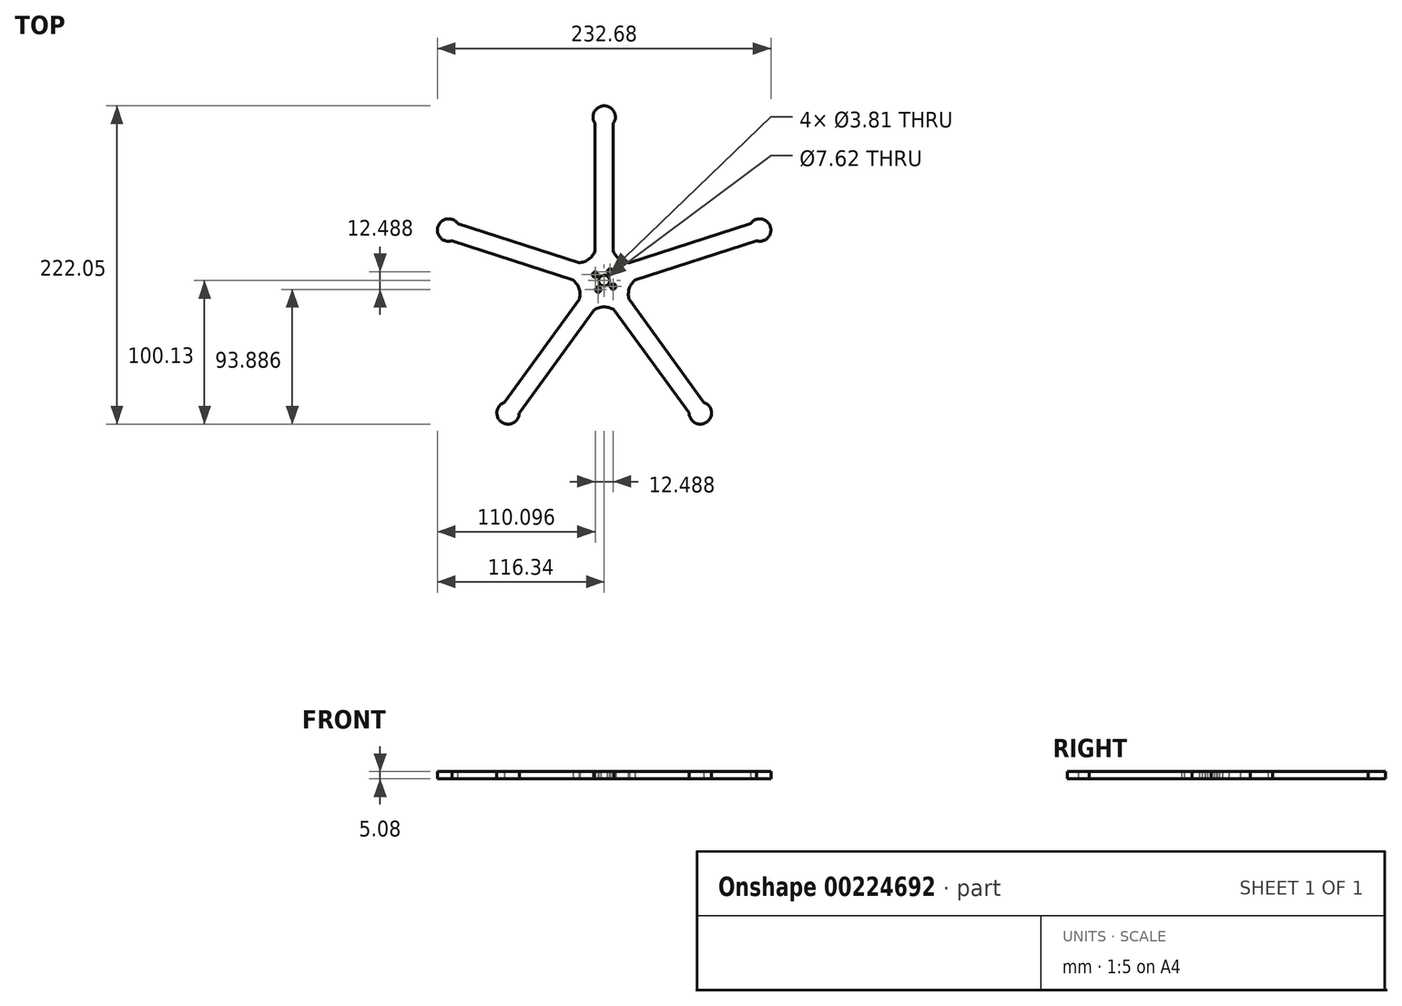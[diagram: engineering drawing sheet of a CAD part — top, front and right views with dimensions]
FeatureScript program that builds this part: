
annotation { "Feature Type Name" : "Feature", "Feature Type Description" : "" }
export const myFeature = defineFeature(function(context is Context, id is Id, definition is map)
    precondition{}
    {
        {
            var Q0;
            Q0=qCreatedBy(makeId("Top.planeOp"),FACE);
            var sketch = newSketch(context, id + "F0", { "sketchPlane" : qUnion([Q0])});
            skArc(sketch, "E0", {"start": v(-17.7, 16.66) * mm, "mid": v(-10.8, 19.1) * mm, "end": v(-6.35, 24.9) * mm});
            skLineSegment(sketch, "E1", {"start": v(-6.35, 24.9) * mm, "end": v(-6.35, 113.8) * mm});
            skLineSegment(sketch, "E2", {"start": v(6.35, 113.8) * mm, "end": v(6.35, 24.9) * mm});
            skArc(sketch, "E3.4.0", {"start": v(6.35, 113.8) * mm, "mid": v(0, 126.15) * mm, "end": v(-6.35, 113.8) * mm});
            skLineSegment(sketch, "E4.1.2", {"start": v(-102.25, 44.13) * mm, "end": v(-17.7, 16.66) * mm});
            skArc(sketch, "E4.1.3", {"start": v(-17.29, -8.76) * mm, "mid": v(-17.48, -1.45) * mm, "end": v(-21.62, 4.58) * mm});
            skLineSegment(sketch, "E4.1.5", {"start": v(-21.62, 4.58) * mm, "end": v(-106.17, 32.05) * mm});
            skLineSegment(sketch, "E4.2.2", {"start": v(-69.54, -80.68) * mm, "end": v(-17.29, -8.76) * mm});
            skArc(sketch, "E4.2.3", {"start": v(7.01, -16.23) * mm, "mid": v(0, -14.15) * mm, "end": v(-7.01, -16.23) * mm});
            skLineSegment(sketch, "E4.2.5", {"start": v(-7.01, -16.23) * mm, "end": v(-59.27, -88.15) * mm});
            skLineSegment(sketch, "E4.3.2", {"start": v(59.27, -88.15) * mm, "end": v(7.01, -16.23) * mm});
            skArc(sketch, "E4.3.3", {"start": v(21.62, 4.58) * mm, "mid": v(17.48, -1.45) * mm, "end": v(17.29, -8.76) * mm});
            skLineSegment(sketch, "E4.3.5", {"start": v(17.29, -8.76) * mm, "end": v(69.54, -80.68) * mm});
            skLineSegment(sketch, "E4.4.2", {"start": v(106.17, 32.05) * mm, "end": v(21.62, 4.58) * mm});
            skArc(sketch, "E4.4.3", {"start": v(6.35, 24.9) * mm, "mid": v(10.8, 19.1) * mm, "end": v(17.7, 16.66) * mm});
            skLineSegment(sketch, "E4.4.5", {"start": v(17.7, 16.66) * mm, "end": v(102.25, 44.13) * mm});
            skPoint(sketch, "E4.center", {"position": v(0, 4.23) * mm});
            skArc(sketch, "E5.1.0", {"start": v(-102.25, 44.13) * mm, "mid": v(-115.96, 41.9) * mm, "end": v(-106.17, 32.05) * mm});
            skArc(sketch, "E5.2.0", {"start": v(-69.54, -80.68) * mm, "mid": v(-71.67, -94.4) * mm, "end": v(-59.27, -88.15) * mm});
            skArc(sketch, "E5.3.0", {"start": v(59.27, -88.15) * mm, "mid": v(71.67, -94.4) * mm, "end": v(69.54, -80.68) * mm});
            skArc(sketch, "E5.4.0", {"start": v(106.17, 32.05) * mm, "mid": v(115.96, 41.9) * mm, "end": v(102.25, 44.13) * mm});
            skCircle(sketch, "E6", {"center": v(-6.24, 8.37) * mm, "radius": 1.9 * mm});
            skCircle(sketch, "E7", {"center": v(0, 4.23) * mm, "radius": 3.81 * mm});
            skCircle(sketch, "E8.1.0", {"center": v(-4.14, -2.01) * mm, "radius": 1.9 * mm});
            skCircle(sketch, "E8.2.0", {"center": v(6.24, 0.09) * mm, "radius": 1.9 * mm});
            skCircle(sketch, "E8.3.0", {"center": v(4.14, 10.47) * mm, "radius": 1.9 * mm});
            skSolve(sketch);
        }
        {
            var Q0;
            Q0=makeQuery(id+"F0.imprint","IMPRINT",FACE,{"disambiguationData":[TD([[makeQuery(id+"F0.imprint","IMPRINT",EDGE,{"derivedFrom":sQuery(id+"F0.wireOp",EDGE,"E0")}),-1.0]])]});
            extrude(context, id + "F1", {"entities" : qUnion([Q0]), "depth" : 5.08 * mm, "offsetDistance" : 25.4 * mm});
        }
    });
